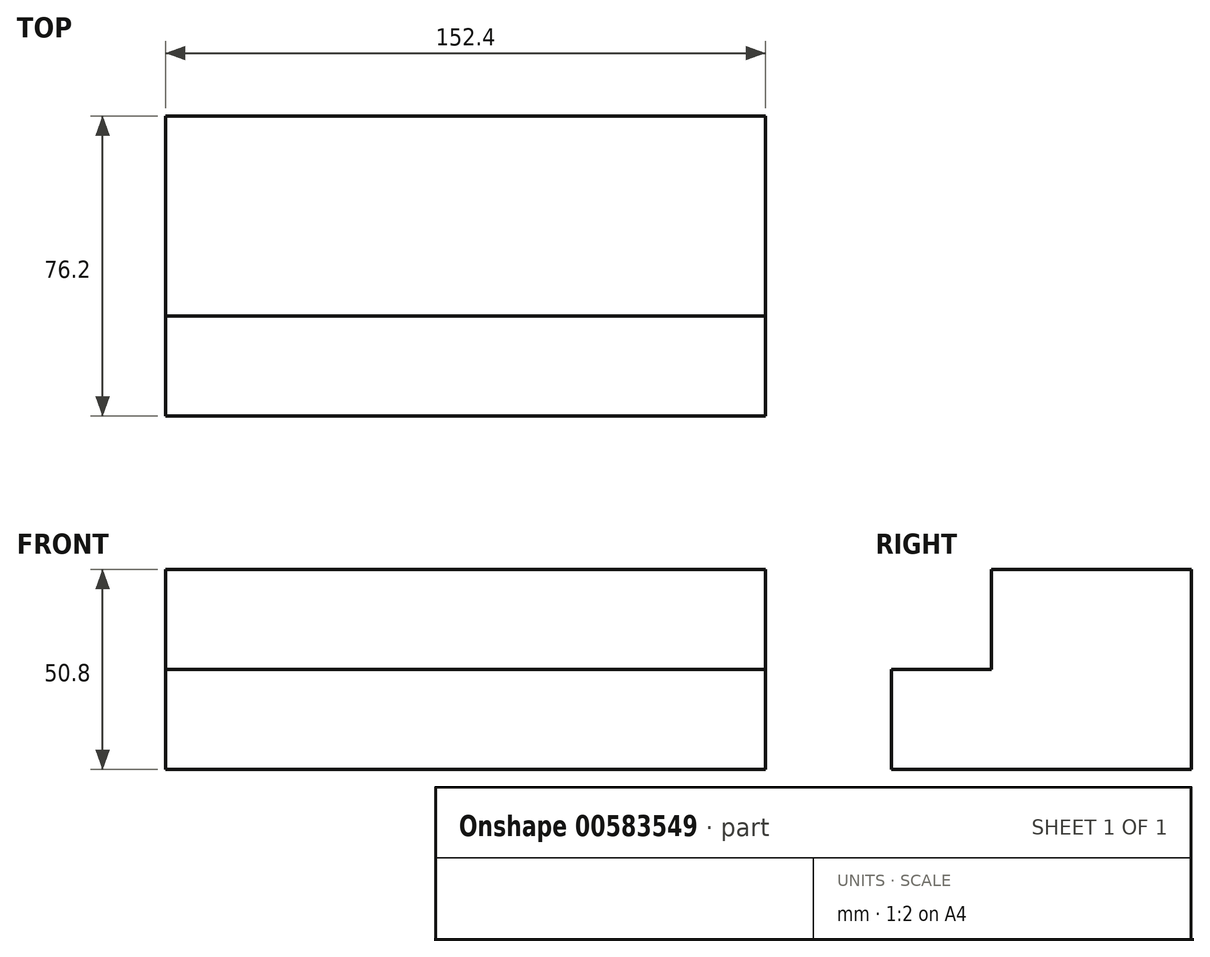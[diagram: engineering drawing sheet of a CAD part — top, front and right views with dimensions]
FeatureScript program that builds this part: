
annotation { "Feature Type Name" : "Feature", "Feature Type Description" : "" }
export const myFeature = defineFeature(function(context is Context, id is Id, definition is map)
    precondition{}
    {
        {
            var Q0;
            Q0=qCreatedBy(makeId("Right.planeOp"),FACE);
            var sketch = newSketch(context, id + "F0", { "sketchPlane" : qUnion([Q0])});
            skLineSegment(sketch, "E0", {"start": v(0, 0) * mm, "end": v(0, 25.4) * mm});
            skLineSegment(sketch, "E1", {"start": v(0, 25.4) * mm, "end": v(25.4, 25.4) * mm});
            skLineSegment(sketch, "E2", {"start": v(25.4, 25.4) * mm, "end": v(25.4, 50.8) * mm});
            skLineSegment(sketch, "E3", {"start": v(25.4, 50.8) * mm, "end": v(76.2, 50.8) * mm});
            skLineSegment(sketch, "E4", {"start": v(76.2, 50.8) * mm, "end": v(76.2, 0) * mm});
            skLineSegment(sketch, "E5", {"start": v(76.2, 0) * mm, "end": v(0, 0) * mm});
            skSolve(sketch);
        }
        {
            var Q0;
            Q0=makeQuery(id+"F0.imprint","IMPRINT",FACE,{"disambiguationData":[TD([[makeQuery(id+"F0.imprint","IMPRINT",EDGE,{"derivedFrom":sQuery(id+"F0.wireOp",EDGE,"E0")}),-1.0]])]});
            extrude(context, id + "F1", {"entities" : qUnion([Q0]), "depth" : 152.4 * mm, "offsetDistance" : 25.4 * mm});
        }
    });
